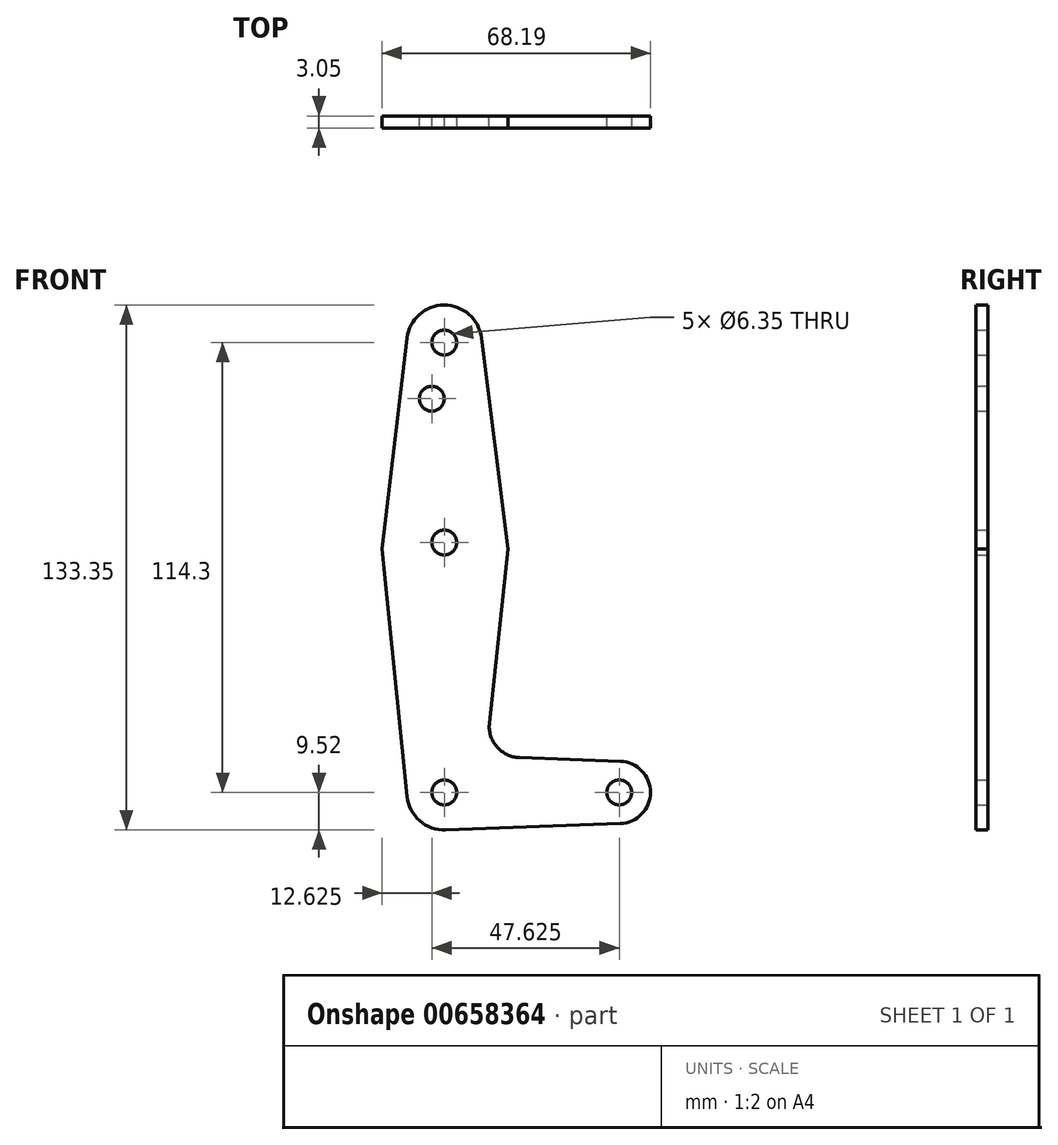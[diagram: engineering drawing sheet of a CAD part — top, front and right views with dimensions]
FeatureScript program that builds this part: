
annotation { "Feature Type Name" : "Feature", "Feature Type Description" : "" }
export const myFeature = defineFeature(function(context is Context, id is Id, definition is map)
    precondition{}
    {
        {
            var Q0;
            Q0=qCreatedBy(makeId("Front.planeOp"),FACE);
            var sketch = newSketch(context, id + "F0", { "sketchPlane" : qUnion([Q0])});
            skLineSegment(sketch, "E0", {"start": v(0, 114.3) * mm, "end": v(0, 0) * mm, "construction": true});
            skLineSegment(sketch, "E1", {"start": v(0, 0) * mm, "end": v(44.45, 0) * mm, "construction": true});
            skCircle(sketch, "E2", {"center": v(0, 114.3) * mm, "radius": 9.53 * mm});
            skCircle(sketch, "E3", {"center": v(0, 63.5) * mm, "radius": 15.88 * mm});
            skCircle(sketch, "E4", {"center": v(0, 0) * mm, "radius": 9.53 * mm});
            skCircle(sketch, "E5", {"center": v(44.45, 0) * mm, "radius": 7.94 * mm});
            skLineSegment(sketch, "E6", {"start": v(-9.46, 115.42) * mm, "end": v(-15.8, 61.91) * mm});
            skLineSegment(sketch, "E7", {"start": v(-15.8, 61.91) * mm, "end": v(-9.48, -0.95) * mm});
            skLineSegment(sketch, "E8", {"start": v(9.45, 115.5) * mm, "end": v(16.2, 61.91) * mm});
            skLineSegment(sketch, "E9", {"start": v(16.2, 61.91) * mm, "end": v(11.47, 17.64) * mm});
            skLineSegment(sketch, "E10", {"start": v(19.09, 8.85) * mm, "end": v(44.73, 7.93) * mm});
            skLineSegment(sketch, "E11", {"start": v(0.34, -9.52) * mm, "end": v(44.73, -7.93) * mm});
            skCircle(sketch, "E12", {"center": v(0, 114.3) * mm, "radius": 3.18 * mm});
            skCircle(sketch, "E13", {"center": v(0, 63.5) * mm, "radius": 3.18 * mm});
            skCircle(sketch, "E14", {"center": v(0, 0) * mm, "radius": 3.18 * mm});
            skCircle(sketch, "E15", {"center": v(44.45, 0) * mm, "radius": 3.18 * mm});
            skArc(sketch, "E16.filletArc", {"start": v(11.47, 17.64) * mm, "mid": v(13.36, 11.58) * mm, "end": v(19.09, 8.85) * mm});
            skCircle(sketch, "E17", {"center": v(-3.18, 100.03) * mm, "radius": 3.18 * mm});
            skSolve(sketch);
        }
        {
            var Q0;
            Q0=makeQuery(id+"F0.imprint","IMPRINT",FACE,{"disambiguationData":[TD([[makeQuery(id+"F0.imprint","IMPRINT",EDGE,{"derivedFrom":sQuery(id+"F0.wireOp",EDGE,"E12")}),-1.0]])]});
            var Q1;
            Q1=makeQuery(id+"F0.imprint","IMPRINT",FACE,{"disambiguationData":[TD([[makeQuery(id+"F0.imprint","IMPRINT",EDGE,{"derivedFrom":sQuery(id+"F0.wireOp",EDGE,"E17")}),-1.0]])]});
            var Q2;
            Q2=makeQuery(id+"F0.imprint","IMPRINT",FACE,{"disambiguationData":[TD([[makeQuery(id+"F0.imprint","IMPRINT",EDGE,{"derivedFrom":sQuery(id+"F0.wireOp",EDGE,"E13")}),-1.0]])]});
            var Q3;
            {var subQ3=sQuery(id+"F0.wireOp",EDGE,"E7");Q3=makeQuery(id+"F0.imprint","IMPRINT",FACE,{"disambiguationData":[TD([[makeQuery(id+"F0.imprint","IMPRINT",EDGE,{"derivedFrom":subQ3}),1.0]])]});}
            var Q4;
            Q4=makeQuery(id+"F0.imprint","IMPRINT",FACE,{"disambiguationData":[TD([[makeQuery(id+"F0.imprint","IMPRINT",EDGE,{"derivedFrom":sQuery(id+"F0.wireOp",EDGE,"E14")}),-1.0]])]});
            var Q5;
            Q5=makeQuery(id+"F0.imprint","IMPRINT",FACE,{"disambiguationData":[TD([[makeQuery(id+"F0.imprint","IMPRINT",EDGE,{"derivedFrom":sQuery(id+"F0.wireOp",EDGE,"E15")}),-1.0]])]});
            extrude(context, id + "F1", {"entities" : qUnion([Q0, Q1, Q2, Q3, Q4, Q5]), "depth" : 3.05 * mm, "offsetDistance" : 25.4 * mm});
        }
    });
